# Revit family: QF_ELECTROLUXPROFESSIONAL_1LSNJ4_IC64821_G
name_source: partatom
category: Attrezzature speciali
units: mm (PartAtom-declared; Revit-internal decimal feet)

## family parameters
Basato su piano di lavoro = No
Condiviso = No
Punto di calcolo locali = No
Quota connettore circolare = Usa diametro
Sempre verticale = Sì
Taglio con vuoti quando caricato = No
Tipo di parte = Normale

## types (8) — shared parameters
Gas KW = 44
Latent Heat Output = 0.0
Modello = IC64821
Phase = 3
Produttore = Electrolux Professional
Sensible Heat Output = 0.0
URL = www.electroluxprofessional.com
zero-valued in all types: Prospetto di default, Steam Pounds per Hour

## per-type parameters (varying)
| type | Cycle | Depth Actual | Descrizione | Height Actual | Item Number | Length Actual | Volts | Watts | Weight |
| 9882030204 | 50 Hz | 1110 mm  [stored 3.64173 ft] | IRONER CYLINDER IC64821 2120MM ACTIVE GAS CE 400/50/3 6MM SST CYL. FR FEED NOW | 1270 mm  [stored 4.16667 ft] | 1L8273 | 2775 mm  [stored 9.10433 ft] | 400 V | 1000 W | 945 |
| 9882030150 | 50 Hz | 1110 mm  [stored 3.64173 ft] | IRONER CYLINDER IC64821 2120MM PERFORMANCE GAS CE 400/50/3 DUBIXIUM ML VAC.FEED.TABLE | 1270 mm  [stored 4.16667 ft] | 1L0GS7 | 2775 mm  [stored 9.10433 ft] | 400 V | 1000 W | 945 |
| 9882030322 | 50 Hz | 0 mm  [stored 0 ft] | IRONER CYLINDER IC64821 2120MM GAS CE 400/50/3 6MM SST CYL. ML DIAMMS CLUTCH | 0 mm  [stored 0 ft] | 1LT6UJ | 0 mm  [stored 0 ft] | 400 V | 1000 W | 0 |
| 9882030151 | 50 Hz | 1110 mm  [stored 3.64173 ft] | IRONER CYLINDER IC64821 2120MM PERFORMANCE GAS CE 400/50/3 DUBIXIUM FR VAC.FEED.TABLE | 1270 mm  [stored 4.16667 ft] | 1L0GPK | 2775 mm  [stored 9.10433 ft] | 400 V | 1000 W | 945 |
| 9882030315 | 50 Hz | 1110 mm  [stored 3.64173 ft] | IRONER CYLINDER IC64821 2120MM ACTIVE GAS CE 230/50/3 6MM SST CYL. EN-ES-PO FEED NOW | 1270 mm  [stored 4.16667 ft] | 1LT6BT | 2775 mm  [stored 9.10433 ft] | 230 V | 1400 W | 945 |
| 9882030268 | 60 Hz | 1110 mm  [stored 3.64173 ft] | IRONER CYLINDER IC64821 2120MM ACTIVE GAS CE 208-240/60/3 6MM SST CYL. EN, ES, PO FEED NOW | 1270 mm  [stored 4.16667 ft] | 1L0H48 | 2775 mm  [stored 9.10433 ft] | 240 V | 1400 W | 945 |
| 9882030205 | 50 Hz | 1110 mm  [stored 3.64173 ft] | IRONER CYLINDER IC64821 2120MM ACTIVE GAS CE 400/50/3 6MM SST CYL. ML FEED NOW | 1270 mm  [stored 4.16667 ft] | 1L8274 | 2775 mm  [stored 9.10433 ft] | 400 V | 1000 W | 945 |
| 9882030232 | 50 Hz | 1110 mm  [stored 3.64173 ft] | IRONER CYLINDER IC64821 2120MM GAS CE 400/50/3 DUBIXIUM ML VAC.FEED.TABLE DIAMMS | 1270 mm  [stored 4.16667 ft] | 1LA25D | 2775 mm  [stored 9.10433 ft] | 400 V | 1000 W | 945 |

note: [stored X ft] marks values corroborated as IEEE doubles in the binary element streams (Revit-internal decimal feet)

## geometry (parser evidence)
native form markers: Sweep x11
no freeform markers — native parametric forms only
